# Revit family: Faucet-Wall_Mount-American_Standard-Yoke-8345.115
name_source: partatom
category: Plumbing Fixtures
revit_build: Autodesk Revit 2014 (Build: 20130308_1515(x64)
units: mm (PartAtom-declared; Revit-internal decimal feet)

## types (1)
- 8345.115
    ADA Compliant = Yes
    Assembly Code = D2020300
    CW Connection = Yes
    CWFU = 1.5
    Cold Water Connection Diameter = 0' - 0 1/2"
    Description = Exposed Yoke Wall-Mount Utility Faucet With Bottom Fork Brace and Offset Shanks.
    HW Connection = Yes
    HWFU = 1.5
    Height = 0' - 5 1/2"
    Hot Water Connection Diameter = 0' - 0 1/2"
    Length = 1' - 4 3/16"
    Manufacturer = American Standard
    Material = Polished-American Standard-002-Chrome
    Model = 8345.115
    Product Documentation Link = https://www.americanstandard-us.com
    Product URL = https://www.americanstandard-us.com
    Revised Date = 02/09/2017
    Specification = Exposed Yoke Wall-Mount Utility Faucet. Bottom fork brace. Cast brass spout with plain end. Ceramic disc valves. Integral supply stops. Offset shanks with integral check valves. Vandal-resistant Wrist Blade Handles. Bucket hook. 1/2" NPT female inlets. Adjustable centers-to-centers: 6"-10" (152 - 254 mm).
    URL = http://www.americanstandard-us.com
    Vent Connection = No
    WFU = 0
    Waste Connection = No
    Width = 1' - 3 3/4"

## geometry (parser evidence)
native form markers: Sweep x1
no freeform markers — native parametric forms only
